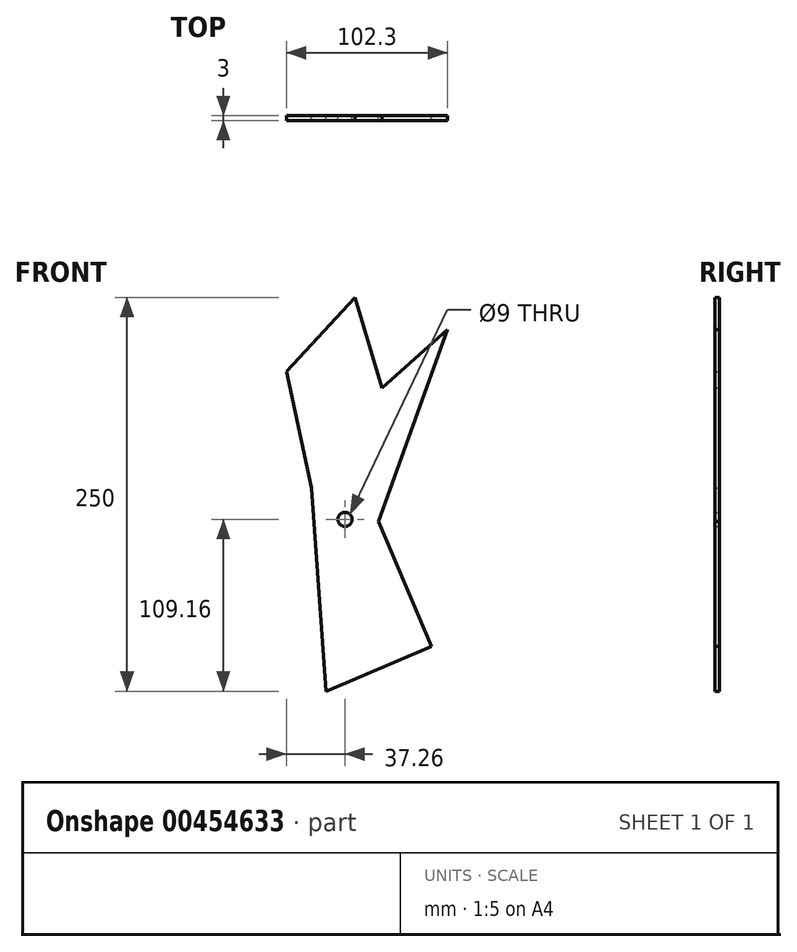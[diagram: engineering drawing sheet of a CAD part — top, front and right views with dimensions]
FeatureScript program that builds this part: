
annotation { "Feature Type Name" : "Feature", "Feature Type Description" : "" }
export const myFeature = defineFeature(function(context is Context, id is Id, definition is map)
    precondition{}
    {
        {
            var Q0;
            Q0=qCreatedBy(makeId("Front.planeOp"),FACE);
            var sketch = newSketch(context, id + "F0", { "sketchPlane" : qUnion([Q0])});
            skLineSegment(sketch, "E0", {"start": v(-21.17, 20.02) * mm, "end": v(-37.26, 93.78) * mm});
            skLineSegment(sketch, "E1", {"start": v(-37.26, 93.78) * mm, "end": v(6.45, 140.84) * mm});
            skLineSegment(sketch, "E2", {"start": v(6.45, 140.84) * mm, "end": v(23.45, 83.46) * mm});
            skLineSegment(sketch, "E3", {"start": v(23.45, 83.46) * mm, "end": v(65.04, 120.5) * mm});
            skLineSegment(sketch, "E4", {"start": v(65.04, 120.5) * mm, "end": v(21.32, -1.23) * mm});
            skLineSegment(sketch, "E5", {"start": v(21.32, -1.23) * mm, "end": v(55.02, -80.76) * mm});
            skLineSegment(sketch, "E6", {"start": v(55.02, -80.76) * mm, "end": v(-12.01, -109.16) * mm});
            skLineSegment(sketch, "E7", {"start": v(-12.01, -109.16) * mm, "end": v(-21.17, 20.02) * mm});
            skCircle(sketch, "E8", {"center": v(0, 0) * mm, "radius": 4.5 * mm});
            skSolve(sketch);
        }
        {
            var Q0;
            Q0=makeQuery(id+"F0.imprint","IMPRINT",FACE,{"disambiguationData":[TD([[makeQuery(id+"F0.imprint","IMPRINT",EDGE,{"derivedFrom":sQuery(id+"F0.wireOp",EDGE,"E0")}),-1.0]])]});
            extrude(context, id + "F1", {"entities" : qUnion([Q0]), "depth" : 3 * mm});
        }
    });
